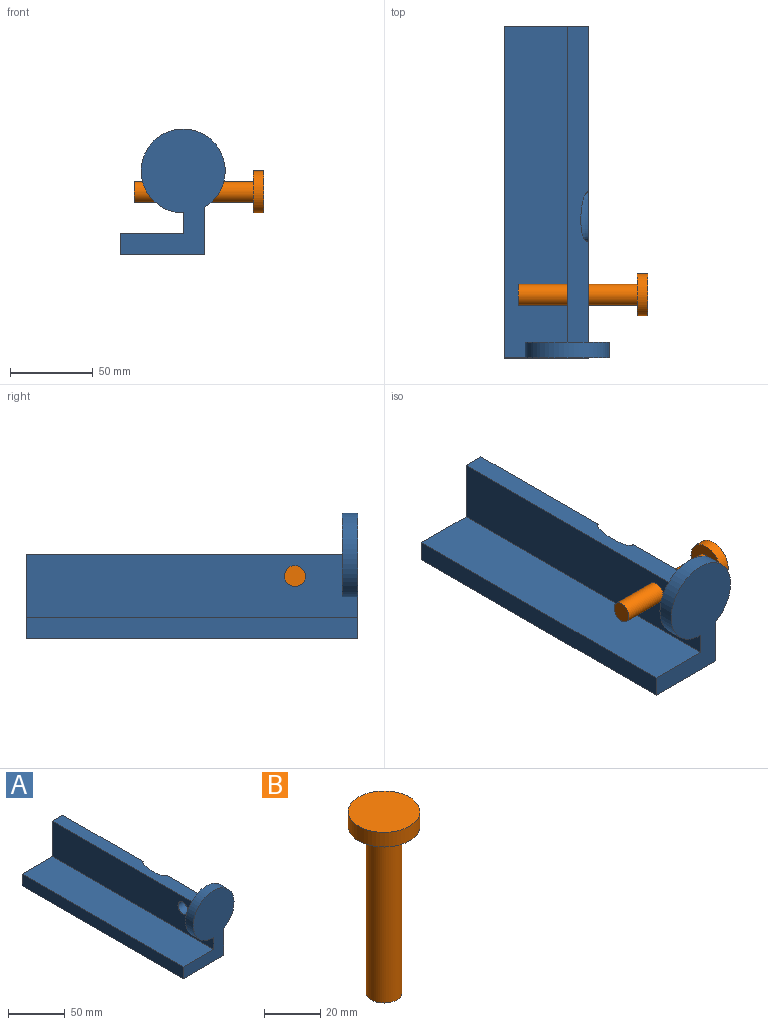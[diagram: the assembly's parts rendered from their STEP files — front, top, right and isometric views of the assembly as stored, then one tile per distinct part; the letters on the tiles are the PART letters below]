
ASSEMBLY  parts=2 mates=1
PART A: 15 faces, bbox 69.5x206.6x82.2 mm
  f0: plane 191.14x12.7mm, normal (0,0,1), area 2320mm2, adj f4,f5,f7,f10,f13
  f1: plane 200.66x38.1mm, normal (0,0,1), area 7645.1mm2, adj f2,f5,f6,f7
  f2: plane 200.66x12.7mm, normal (-1,0,0), area 2548.4mm2, adj f1,f3,f6,f7
  f3: plane 200.66x50.8mm, normal (0,0,-1), area 10193.5mm2, adj f2,f4,f6,f7
  f4: plane 206.61x56.75mm, normal (1,0,0), area 7641.5mm2, adj f0,f3,f6,f7,f8,f9,f10,f11
  f5: plane 200.66x38.1mm, normal (-1,0,0), area 7276.5mm2, adj f0,f1,f6,f7,f8,f9,f10
  f6: plane 76.2x63.5mm, normal (0,-1,0), area 2847.3mm2, adj f1,f2,f3,f4,f5,f9
  f7: plane 50.8x50.8mm, normal (0,1,0), area 1129mm2, adj f0,f1,f2,f3,f4,f5
  f8: cylinder r=6.35mm len=12.7mm, axis (1,0,0), area 506.7mm2, adj f4,f5
  f9: cylinder r=25.4mm len=50.8mm, axis (0,-1,0), area 1393.4mm2, adj f4,f5,f6,f10
  f10: plane 50.8x50.8mm, normal (0,1,0), area 1718.2mm2, adj f0,f4,f5,f9
  f11: plane 2.39x1.27mm, normal (0,-0.94,0.34), area 2.5mm2, adj f4,f14
  f12: plane 13.57x8.15mm, normal (0,-0.93,-0.38), area 63.3mm2, adj f4,f13
  f13: bspline ~124.36x43.93mm, area 3337.6mm2, adj f0,f4,f12,f14
  f14: bspline ~13.68x9.06mm, area 112.9mm2, adj f4,f11,f13
PART B: 5 faces, bbox 25.4x25.4x78.5 mm
  f0: cylinder r=6.35mm len=72.14mm, axis (0,0,-1), area 2878.1mm2, adj f1,f4
  f1: plane 12.7x12.7mm, normal (0,0,-1), area 126.7mm2, adj f0
  f2: cylinder r=12.7mm len=25.4mm, axis (0,0,-1), area 506.7mm2, adj f3,f4
  f3: plane 25.4x25.4mm, normal (0,0,1), area 506.7mm2, adj f2
  f4: plane 25.4x25.4mm, normal (0,0,-1), area 380mm2, adj f0,f2
PLACE A t=(-54.23,8.64,10.61)mm fixed
PLACE B rot(axis=(0.7,0.13,0.7),164.9deg) t=(-45.85,-42.16,36.01)mm
MATE revolute B.f0 <-> A.f8  axis (-1,0,0) through (-9.78,-42.16,36.01)mm
